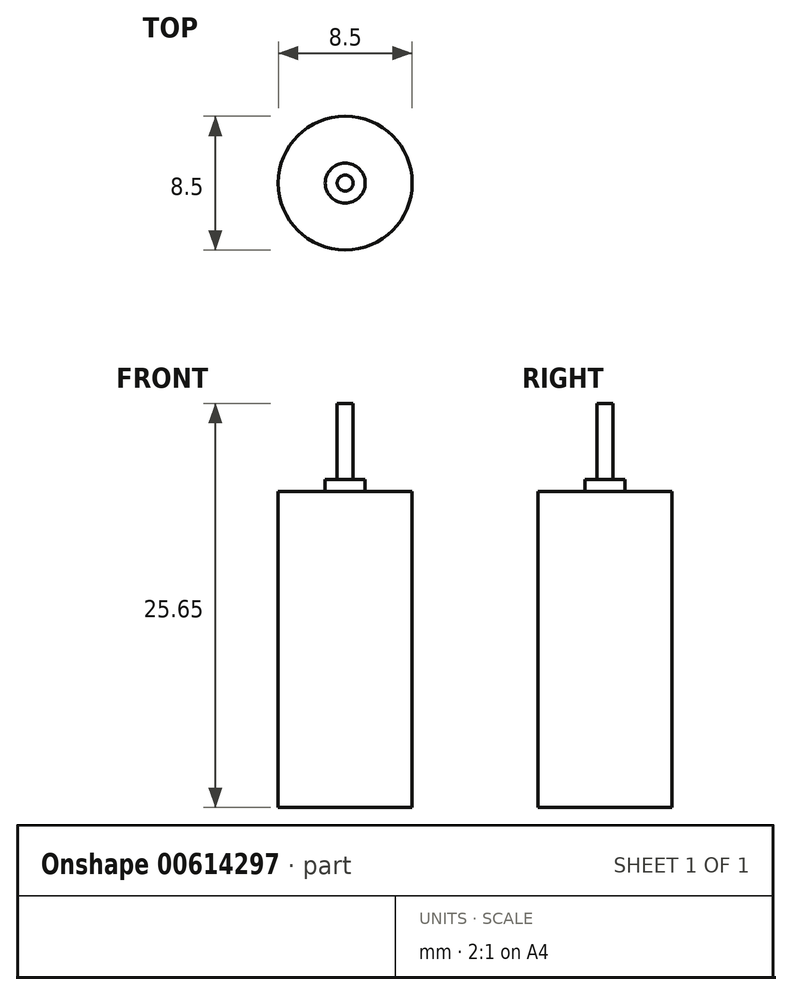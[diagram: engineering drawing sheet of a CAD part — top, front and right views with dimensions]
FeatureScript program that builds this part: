
annotation { "Feature Type Name" : "Feature", "Feature Type Description" : "" }
export const myFeature = defineFeature(function(context is Context, id is Id, definition is map)
    precondition{}
    {
        {
            var Q0;
            Q0=qCreatedBy(makeId("Top.planeOp"),FACE);
            var sketch = newSketch(context, id + "F0", { "sketchPlane" : qUnion([Q0])});
            skCircle(sketch, "E0", {"center": v(0, 0) * mm, "radius": 4.25 * mm});
            skSolve(sketch);
        }
        {
            var Q0;
            Q0=makeQuery(id+"F0.imprint","IMPRINT",FACE,{"disambiguationData":[TD([[makeQuery(id+"F0.imprint","IMPRINT",EDGE,{"derivedFrom":sQuery(id+"F0.wireOp",EDGE,"E0")}),1.0]])]});
            extrude(context, id + "F1", {"entities" : qUnion([Q0]), "depth" : 20.07 * mm, "offsetDistance" : 25.4 * mm});
        }
        {
            var Q0;
            Q0=makeQuery(id+"F1.opExtrude","CAP_FACE",FACE,{"disambiguationData":[OSD([sQuery(id+"F0.wireOp",EDGE,"E0")])],"isStart":false});
            var sketch = newSketch(context, id + "F2", { "sketchPlane" : qUnion([Q0])});
            skCircle(sketch, "E1", {"center": v(0, 0) * mm, "radius": 1.27 * mm});
            skSolve(sketch);
        }
        {
            var Q0;
            Q0=makeQuery(id+"F2.imprint","IMPRINT",FACE,{"disambiguationData":[TD([[makeQuery(id+"F2.imprint","IMPRINT",EDGE,{"derivedFrom":sQuery(id+"F2.wireOp",EDGE,"E1")}),1.0]])]});
            extrude(context, id + "F3", {"entities" : qUnion([Q0]), "operationType" : NewBodyOperationType.ADD, "depth" : 0.76 * mm, "offsetDistance" : 25.4 * mm});
        }
        {
            var Q0;
            Q0=makeQuery(id+"F3.opExtrude","CAP_FACE",FACE,{"disambiguationData":[OSD([sQuery(id+"F2.wireOp",EDGE,"E1")])],"isStart":false});
            var sketch = newSketch(context, id + "F4", { "sketchPlane" : qUnion([Q0])});
            skCircle(sketch, "E2", {"center": v(0, 0) * mm, "radius": 0.5 * mm});
            skSolve(sketch);
        }
        {
            var Q0;
            Q0 = qSketchRegion(id + "F4", true);
            extrude(context, id + "F5", {"entities" : qUnion([Q0]), "operationType" : NewBodyOperationType.ADD, "depth" : 4.83 * mm, "offsetDistance" : 25.4 * mm});
        }
    });
